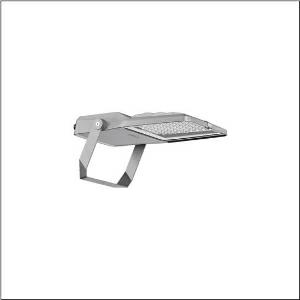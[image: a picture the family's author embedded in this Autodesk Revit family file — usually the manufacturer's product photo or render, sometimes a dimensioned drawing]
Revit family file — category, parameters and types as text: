
# Revit family: floodlight_fl_21_iq_mini___pl64_5xa7772d4e1a_07d3
name_source: partatom
category: Lighting Fixtures
units: mm (PartAtom-declared; Revit-internal decimal feet)

## family parameters
Cut with Voids When Loaded = No
Host = Face
Light Source = No
Part Type = Normal
Room Calculation Point = No
Round Connector Dimension = Use Diameter
Shared = No

## types (1)
- --- (1 x LED, 17970 lm, 143 W, 4000K)
    Apparent Load = 143 VA
    CIE Flux Codes = 28 80 98 100 100
    Color Rendering = 70
    Color Temperature = 4000K
    Default Elevation = 1800 mm
    Description = Floodlight FL 21 iQ mini, floodlight, primary light control with lens, of PMMA, primary optical cover: protective disc, of toughened safety glass, transparent, light distribution: PL64, light emission: direct distribution, installation type: surface-mounted, LED, High Power LED, rated luminous flux: 17.970lm, luminous efficacy: 126lm/W, light colour: 740, colour temperature: 4000K, control gear: iQ Street-Remote/DALI, control: Street-Remote, Auto-Match, Temp-Guard, Night-Set, Smart-Wire, Desk-Remote (wireless, voltage-free reading and setting of iQ features in the workshop via application-optimized NFC function/RFID function), optimised constant luminous flux control (CLO 2.0), with terminal, 6-pole, mains connection: 220..240V, AC, 50/60Hz, start of lifetime: 143W, end of service life: 152W, reduction: 61W, luminaire housing, of diecast aluminium, powder-coated, Siteco® metallic grey (DB 702S), corrosivity category C5 mid according to DIN EN ISO 12944, suitable for swimming pools, chlorine-resistant, sealing non-destructively replaceable, mounting bracket, of steel, galvanised, powder-coated, Siteco® metallic grey (DB 702S), protection rating (complete): IP66, insulation class (complete): insulation class II (safety insulation), certification: CE, ENEC, VDE, protection symbol: D, impact resistance: IK08, permissible operating ambient temperature: -40..+40°C, permissible operating ambient temperature for outdoor applications: -40..+50°C, standard: DIN EN 12944, LABS conformity tested according to VDMA 24364:2018-05, packaging unit: 1 piece

Light Distribution: PL64
    Height = 70 mm
    Lamp = 1 x LED
    Lamp Light Flux = 17970 lm
    Lamp Power = 143 W
    Lamp count = 1
    Length = 485 mm
    Luminous efficacy = 126 lm/W
    Manufacturer = Siteco
    ModVariant = No
    Model = 5XA7772D4E1A
    Number of Poles = 1
    OnlyDefault = Yes
    Power Factor = 1
    Product Name = Floodlight FL 21 iQ mini | PL64
    Product group = floodlight | pylon annexe
    ProductGroupID = 6200
    Protection Class = Protection class II
    Protection Degree = IP 66
    RLX_Detail_Level = 1
    RLX_Emergency_Light_Flux = 0 lm
    RLX_Emergency_Type = 0
    RLX_Emergency_Type_DB = No
    RlxData = <blob elided: 96553 chars, md5=717d5b32>
    Socket = socket
    Standby Power = 0 W
    System Light Flux = 17970 lm
    System Power = 143 W
    Type Comments = factory setting: luminous flux: 100 % | dim-lin: 254 | 730 mA
    Type Image = l_1006845.jpg
    URL = http://relux.com
    VarID = @adj_165726
    Voltage = 0 V
    Weight = 0.00 kg
    Width = 337 mm

## geometry (parser evidence)
native form markers: Blend x4, Sweep x12
no freeform markers — native parametric forms only
